# Revit family: MT-VMS_DB-SG_OX
name_source: partatom
category: Windows
revit_build: Autodesk Revit 2017 (Build: 20160225_1515(x64)
units: mm (PartAtom-declared; Revit-internal decimal feet)

## family parameters
Always vertical = Yes
Cut with Voids When Loaded = No
Host = Wall
OmniClass Number = 23.30.20.00
OmniClass Title = Windows
Room Calculation Point = No
Shared = No

## types (1)
- MT-VMS_DB-SG_OX
    101.6mm FRAME THICKNESS = Yes
    76mm FRAME THICKNESS = No
    AIR POCKET = 5 mm  [stored 0.0164042 ft]
    ANZRC COMPLIANT = YES
    Analytic Construction = <None>
    DOUBLE GLAZED = No
    DOUBLE GLAZED THICKNESS = 15 mm  [stored 0.0492126 ft]
    Default Sill Height = 900 mm  [stored 2.95276 ft]
    FRAME MATERIAL = <By Category>
    GLAZED MATERIAL = Glass
    Height = 1000 mm  [stored 3.28084 ft]
    MAX PANEL HEIGHT = 1600 mm  [stored 5.24934 ft]
    MAX PANEL WIDTH = 1200 mm
    Max Height = 1706 mm  [stored 5.59711 ft]
    Max Width = 2480 mm
    Model = VIEWMAX SLIDING WINDOW
    OFFSET = 30 mm  [stored 0.0984252 ft]
    Rough Height = 1000 mm  [stored 3.28084 ft]
    Rough Width = 2000 mm  [stored 6.56168 ft]
    SINGLE GLAZED THICKNESS = 5 mm  [stored 0.0164042 ft]
    TODAYS DATE = 2/12/2018
    TOLERANCE = 10 mm  [stored 0.0328084 ft]
    URL = WWW.ALSPEC.COM.AU
    VERSION = 2.1
    WARNING = No
    Wall Closure = By host
    Width = 2000 mm  [stored 6.56168 ft]
    YEAR = 2019

note: [stored X ft] marks values corroborated as IEEE doubles in the binary element streams (Revit-internal decimal feet)

## geometry (parser evidence)
native form markers: Extrusion x1, Sweep x45
no freeform markers — native parametric forms only
